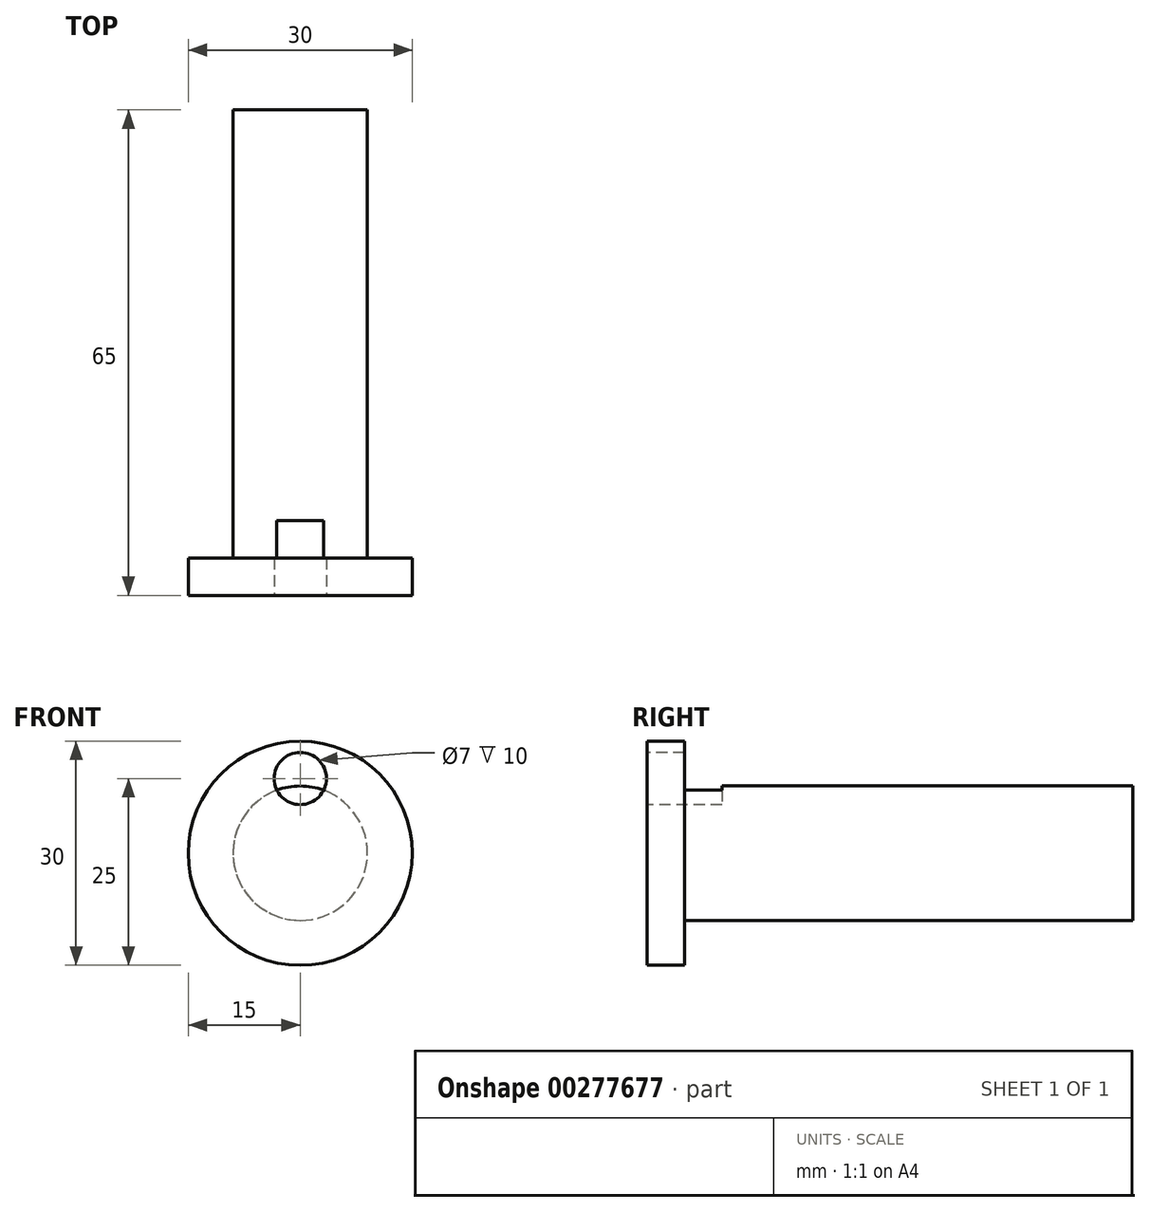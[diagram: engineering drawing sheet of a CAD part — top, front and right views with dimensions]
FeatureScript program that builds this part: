
annotation { "Feature Type Name" : "Feature", "Feature Type Description" : "" }
export const myFeature = defineFeature(function(context is Context, id is Id, definition is map)
    precondition{}
    {
        {
            var Q0;
            Q0=qCreatedBy(makeId("Front.planeOp"),FACE);
            var sketch = newSketch(context, id + "F0", { "sketchPlane" : qUnion([Q0])});
            skCircle(sketch, "E0", {"center": v(0, 0) * mm, "radius": 9 * mm});
            skSolve(sketch);
        }
        {
            var Q0;
            Q0=makeQuery(id+"F0.imprint","IMPRINT",FACE,{"disambiguationData":[TD([[makeQuery(id+"F0.imprint","IMPRINT",EDGE,{"derivedFrom":sQuery(id+"F0.wireOp",EDGE,"E0")}),1.0]])]});
            extrude(context, id + "F1", {"entities" : qUnion([Q0]), "depth" : 60 * mm});
        }
        {
            var Q0;
            Q0=makeQuery(id+"F1.opExtrude","CAP_FACE",FACE,{"disambiguationData":[OSD([sQuery(id+"F0.wireOp",EDGE,"E0")])],"isStart":false});
            var sketch = newSketch(context, id + "F2", { "sketchPlane" : qUnion([Q0])});
            skCircle(sketch, "E1", {"center": v(0, 0) * mm, "radius": 15 * mm});
            skSolve(sketch);
        }
        {
            var Q0;
            Q0=makeQuery(id+"F2.imprint","IMPRINT",FACE,{"disambiguationData":[TD([[makeQuery(id+"F2.imprint","IMPRINT",EDGE,{"derivedFrom":sQuery(id+"F2.wireOp",EDGE,"E1")}),1.0]])]});
            var Q1;
            Q1=makeQuery(id+"F2.imprint","IMPRINT",FACE,{"disambiguationData":[TD([[makeQuery(id+"F2.imprint","IMPRINT",EDGE,{"derivedFrom":makeQuery(id+"F1.opExtrude","CAP_EDGE",EDGE,{"disambiguationData":[OSD([sQuery(id+"F0.wireOp",EDGE,"E0")])],"isStart":false})}),1.0]])]});
            extrude(context, id + "F3", {"entities" : qUnion([Q0, Q1]), "operationType" : NewBodyOperationType.ADD, "depth" : 5 * mm});
        }
        {
            var Q0;
            Q0=makeQuery(id+"F3.opExtrude","CAP_FACE",FACE,{"disambiguationData":[OSD([sQuery(id+"F2.wireOp",EDGE,"E1")])],"isStart":false});
            var sketch = newSketch(context, id + "F4", { "sketchPlane" : qUnion([Q0])});
            skCircle(sketch, "E2", {"center": v(0, 10) * mm, "radius": 3.5 * mm});
            skSolve(sketch);
        }
        {
            var Q0;
            Q0=makeQuery(id+"F4.imprint","IMPRINT",FACE,{"disambiguationData":[TD([[makeQuery(id+"F4.imprint","IMPRINT",EDGE,{"derivedFrom":sQuery(id+"F4.wireOp",EDGE,"E2")}),1.0]])]});
            extrude(context, id + "F5", {"entities" : qUnion([Q0]), "operationType" : NewBodyOperationType.REMOVE, "oppositeDirection" : true, "depth" : 10 * mm});
        }
    });
